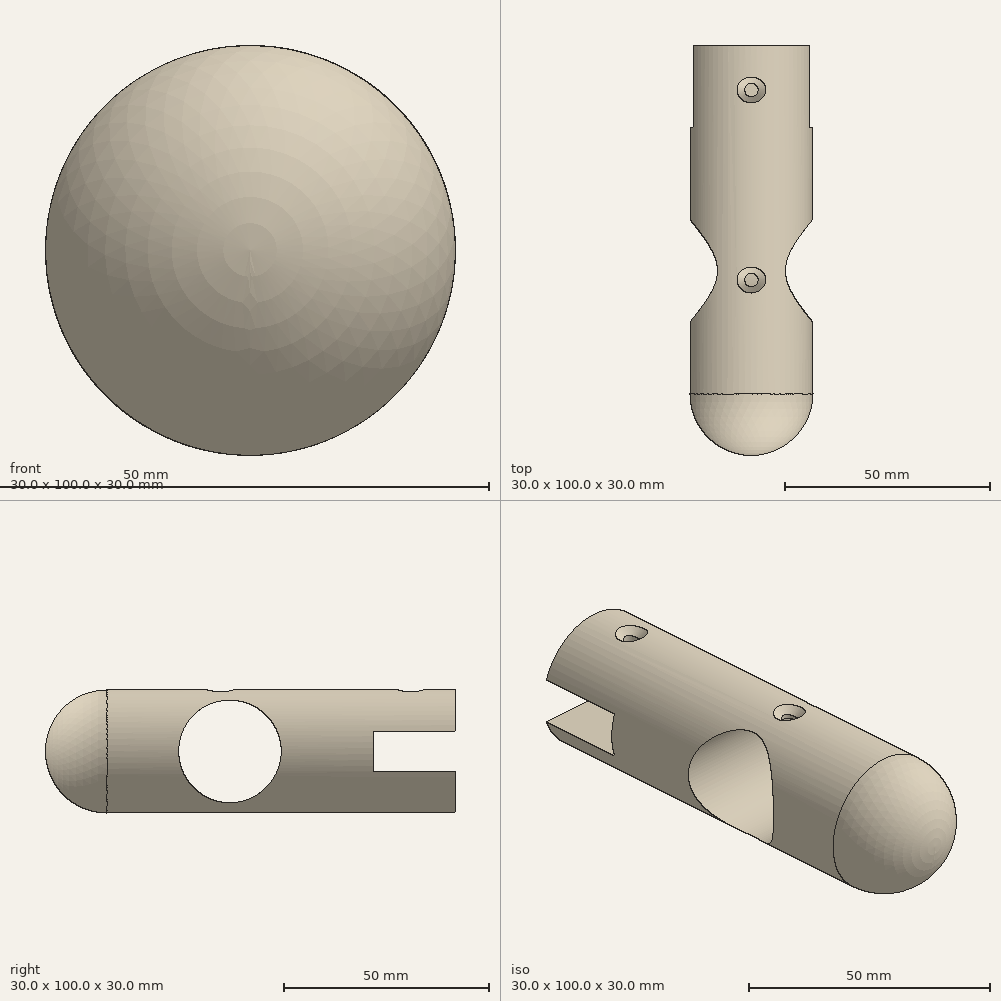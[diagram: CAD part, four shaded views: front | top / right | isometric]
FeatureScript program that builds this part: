
annotation { "Feature Type Name" : "Feature", "Feature Type Description" : "" }
export const myFeature = defineFeature(function(context is Context, id is Id, definition is map)
    precondition{}
    {
        {
            var Q0;
            Q0=qCreatedBy(makeId("Front.planeOp"),FACE);
            var sketch = newSketch(context, id + "F0", { "sketchPlane" : qUnion([Q0])});
            skCircle(sketch, "E0", {"center": v(0, 0) * mm, "radius": 15 * mm});
            skSolve(sketch);
        }
        {
            var Q0;
            Q0=makeQuery(id+"F0.imprint","IMPRINT",FACE,{"disambiguationData":[TD([[makeQuery(id+"F0.imprint","IMPRINT",EDGE,{"derivedFrom":sQuery(id+"F0.wireOp",EDGE,"E0")}),1.0]])]});
            extrude(context, id + "F1", {"entities" : qUnion([Q0]), "depth" : 100 * mm, "offsetDistance" : 25 * mm});
        }
        {
            var Q0;
            Q0=makeQuery(id+"F1.opExtrude","CAP_EDGE",EDGE,{"disambiguationData":[OSD([sQuery(id+"F0.wireOp",EDGE,"E0")])],"isStart":false});
            fillet(context, id + "F2", {"entities" : qUnion([Q0]), "radius" : 15 * mm, "tangentPropagation" : true, "allowEdgeOverflow" : false});
        }
        {
            var Q0;
            Q0=makeQuery(id+"F1.opExtrude","CAP_FACE",FACE,{"disambiguationData":[OSD([sQuery(id+"F0.wireOp",EDGE,"E0")])],"isStart":true});
            var sketch = newSketch(context, id + "F3", { "sketchPlane" : qUnion([Q0])});
            skLineSegment(sketch, "E1", {"start": v(-18.57, 0) * mm, "end": v(22.34, 0) * mm});
            skLineSegment(sketch, "E2.bottom", {"start": v(50, 5) * mm, "end": v(-50, 5) * mm});
            skLineSegment(sketch, "E2.top", {"start": v(50, -5) * mm, "end": v(-50, -5) * mm});
            skLineSegment(sketch, "E2.left", {"start": v(50, 5) * mm, "end": v(50, -5) * mm});
            skLineSegment(sketch, "E2.right", {"start": v(-50, 5) * mm, "end": v(-50, -5) * mm});
            skPoint(sketch, "E2.middle", {"position": v(0, 0) * mm});
            skSolve(sketch);
        }
        {
            var Q0;
            {var subQ0=sQuery(id+"F3.wireOp",EDGE,"E1");var subQ1=makeQuery(id+"F1.opExtrude","CAP_EDGE",EDGE,{"disambiguationData":[OSD([sQuery(id+"F0.wireOp",EDGE,"E0")])],"isStart":true});var subQ2=makeQuery(id+"F3.imprint","INTERSECT",VERTEX,{"disambiguationData":[OD(0.0)],"derivedFrom":[subQ1,subQ0]});Q0=makeQuery(id+"F3.imprint","IMPRINT",FACE,{"disambiguationData":[TD([[makeQuery(id+"F3.imprint","IMPRINT",EDGE,{"disambiguationData":[TD([[subQ2,1.0]])],"derivedFrom":subQ0}),1.0]])]});}
            var Q1;
            {var subQ0=sQuery(id+"F3.wireOp",EDGE,"E1");var subQ1=makeQuery(id+"F1.opExtrude","CAP_EDGE",EDGE,{"disambiguationData":[OSD([sQuery(id+"F0.wireOp",EDGE,"E0")])],"isStart":true});var subQ2=makeQuery(id+"F3.imprint","INTERSECT",VERTEX,{"disambiguationData":[OD(0.0)],"derivedFrom":[subQ1,subQ0]});Q1=makeQuery(id+"F3.imprint","IMPRINT",FACE,{"disambiguationData":[TD([[makeQuery(id+"F3.imprint","IMPRINT",EDGE,{"disambiguationData":[TD([[subQ2,1.0]])],"derivedFrom":subQ0}),-1.0]])]});}
            extrude(context, id + "F4", {"entities" : qUnion([Q0, Q1]), "operationType" : NewBodyOperationType.REMOVE, "oppositeDirection" : true, "depth" : 20 * mm, "offsetDistance" : 25 * mm});
        }
        {
            var Q0;
            Q0=qCreatedBy(makeId("Right.planeOp"),FACE);
            var sketch = newSketch(context, id + "F5", { "sketchPlane" : qUnion([Q0])});
            skCircle(sketch, "E3", {"center": v(-55, 0) * mm, "radius": 12.5 * mm});
            skSolve(sketch);
        }
        {
            var Q0;
            Q0 = qSketchRegion(id + "F5", true);
            extrude(context, id + "F6", {"entities" : qUnion([Q0]), "operationType" : NewBodyOperationType.REMOVE, "oppositeDirection" : true, "depth" : 45 * mm, "offsetDistance" : 25 * mm, "hasSecondDirection" : true, "secondDirectionOppositeDirection" : false, "secondDirectionDepth" : 25 * mm});
        }
        {
            var Q0;
            Q0=qCreatedBy(makeId("Top.planeOp"),FACE);
            var sketch = newSketch(context, id + "F7", { "sketchPlane" : qUnion([Q0])});
            skCircle(sketch, "E4", {"center": v(0, -57.22) * mm, "radius": 1.65 * mm});
            skCircle(sketch, "E5", {"center": v(0, -10.88) * mm, "radius": 1.65 * mm});
            skSolve(sketch);
        }
        {
            var Q0;
            Q0 = qSketchRegion(id + "F7", true);
            extrude(context, id + "F8", {"entities" : qUnion([Q0]), "operationType" : NewBodyOperationType.REMOVE, "depth" : 25 * mm, "offsetDistance" : 25 * mm});
        }
        {
            var Q0;
            Q0=makeQuery(id+"F8.boolean.opBoolean","INTERSECT",EDGE,{"derivedFrom":[makeQuery(id+"F1.opExtrude","SWEPT_FACE",FACE,{"disambiguationData":[OSD([sQuery(id+"F0.wireOp",EDGE,"E0")])]}),makeQuery(id+"F8.opExtrude","SWEPT_FACE",FACE,{"disambiguationData":[OSD([sQuery(id+"F7.wireOp",EDGE,"E4")])]})]});
            var Q1;
            Q1=makeQuery(id+"F8.boolean.opBoolean","INTERSECT",EDGE,{"derivedFrom":[makeQuery(id+"F1.opExtrude","SWEPT_FACE",FACE,{"disambiguationData":[OSD([sQuery(id+"F0.wireOp",EDGE,"E0")])]}),makeQuery(id+"F8.opExtrude","SWEPT_FACE",FACE,{"disambiguationData":[OSD([sQuery(id+"F7.wireOp",EDGE,"E5")])]})]});
            chamfer(context, id + "F9", {"entities" : qUnion([Q0, Q1]), "width" : 1.5 * mm, "tangentPropagation" : true});
        }
    });
